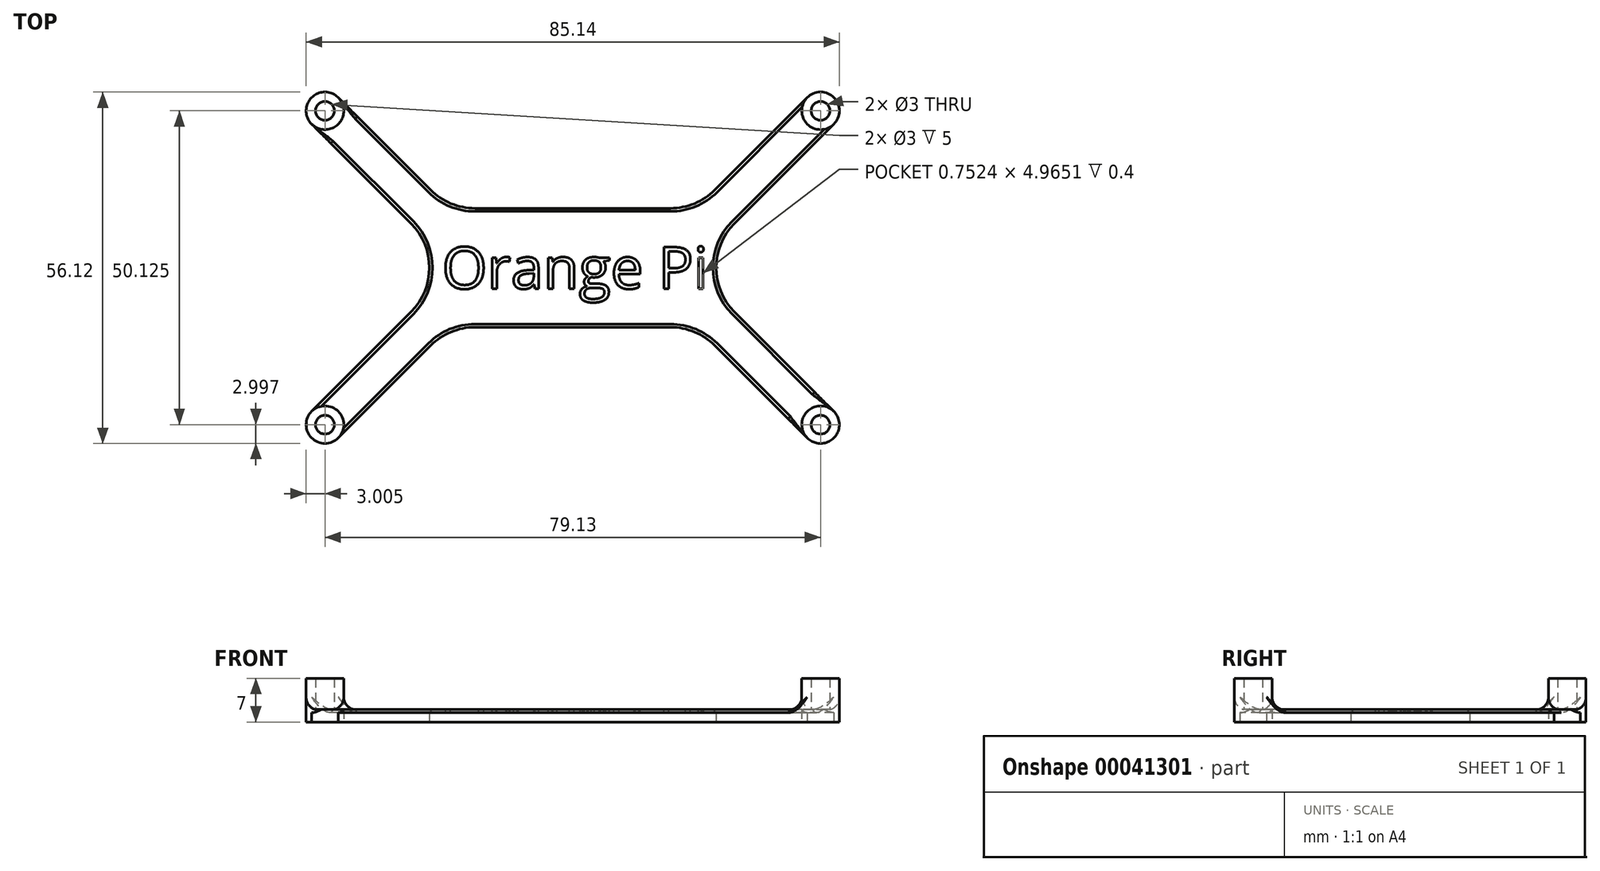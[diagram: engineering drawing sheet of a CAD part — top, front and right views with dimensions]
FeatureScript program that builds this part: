
annotation { "Feature Type Name" : "Feature", "Feature Type Description" : "" }
export const myFeature = defineFeature(function(context is Context, id is Id, definition is map)
    precondition{}
    {
        {
            var Q0;
            Q0=qCreatedBy(makeId("Top.planeOp"),FACE);
            var sketch = newSketch(context, id + "F0", { "sketchPlane" : qUnion([Q0])});
            skLineSegment(sketch, "E0", {"start": v(0, 77.14) * mm, "end": v(0, -73.03) * mm, "construction": true});
            skLineSegment(sketch, "E1", {"start": v(-119.62, 0) * mm, "end": v(131.14, 0) * mm, "construction": true});
            skCircle(sketch, "E2", {"center": v(-39.56, 25.06) * mm, "radius": 3 * mm});
            skLineSegment(sketch, "E3", {"start": v(-37.44, 27.18) * mm, "end": v(-22.69, 12.43) * mm});
            skLineSegment(sketch, "E4", {"start": v(-15.62, 9.5) * mm, "end": v(0, 9.5) * mm});
            skLineSegment(sketch, "E5", {"start": v(-41.69, 22.94) * mm, "end": v(-25.82, 7.07) * mm});
            skCircle(sketch, "E6.MirrorC", {"center": v(39.57, 25.06) * mm, "radius": 3 * mm});
            skLineSegment(sketch, "E7.MirrorCS", {"start": v(37.44, 27.18) * mm, "end": v(22.69, 12.43) * mm});
            skLineSegment(sketch, "E8.MirrorCS", {"start": v(41.69, 22.94) * mm, "end": v(25.82, 7.07) * mm});
            skLineSegment(sketch, "E9.MirrorCS", {"start": v(15.62, 9.5) * mm, "end": v(0, 9.5) * mm});
            skLineSegment(sketch, "E10.MirrorCS", {"start": v(15.62, -9.5) * mm, "end": v(0, -9.5) * mm});
            skLineSegment(sketch, "E11.MirrorCS", {"start": v(41.69, -22.94) * mm, "end": v(25.82, -7.07) * mm});
            skLineSegment(sketch, "E12.MirrorCS", {"start": v(37.44, -27.18) * mm, "end": v(22.69, -12.43) * mm});
            skCircle(sketch, "E13.MirrorC", {"center": v(39.57, -25.06) * mm, "radius": 3 * mm});
            skCircle(sketch, "E14.MirrorC", {"center": v(-39.56, -25.06) * mm, "radius": 3 * mm});
            skLineSegment(sketch, "E15.MirrorCS", {"start": v(-37.44, -27.18) * mm, "end": v(-22.69, -12.43) * mm});
            skLineSegment(sketch, "E16.MirrorCS", {"start": v(-15.62, -9.5) * mm, "end": v(0, -9.5) * mm});
            skLineSegment(sketch, "E17.MirrorCS", {"start": v(-41.69, -22.94) * mm, "end": v(-25.82, -7.07) * mm});
            skPoint(sketch, "E18.visualSharp", {"position": v(-19.76, 9.5) * mm});
            skArc(sketch, "E18.filletArc", {"start": v(-22.69, 12.43) * mm, "mid": v(-19.44, 10.26) * mm, "end": v(-15.62, 9.5) * mm});
            skPoint(sketch, "E19.visualSharp", {"position": v(-18.75, 0) * mm});
            skArc(sketch, "E19.filletArc", {"start": v(-25.82, -7.07) * mm, "mid": v(-22.89, 0) * mm, "end": v(-25.82, 7.07) * mm});
            skPoint(sketch, "E20.visualSharp", {"position": v(-19.76, -9.5) * mm});
            skArc(sketch, "E20.filletArc", {"start": v(-15.62, -9.5) * mm, "mid": v(-19.44, -10.26) * mm, "end": v(-22.69, -12.43) * mm});
            skPoint(sketch, "E21.visualSharp", {"position": v(19.76, -9.5) * mm});
            skArc(sketch, "E21.filletArc", {"start": v(22.69, -12.43) * mm, "mid": v(19.44, -10.26) * mm, "end": v(15.62, -9.5) * mm});
            skPoint(sketch, "E22.visualSharp", {"position": v(18.75, 0) * mm});
            skArc(sketch, "E22.filletArc", {"start": v(25.82, 7.07) * mm, "mid": v(22.89, 0) * mm, "end": v(25.82, -7.07) * mm});
            skPoint(sketch, "E23.visualSharp", {"position": v(19.76, 9.5) * mm});
            skArc(sketch, "E23.filletArc", {"start": v(15.62, 9.5) * mm, "mid": v(19.44, 10.26) * mm, "end": v(22.69, 12.43) * mm});
            skSolve(sketch);
        }
        {
            var Q0;
            {var subQ0=sQuery(id+"F0.wireOp",EDGE,"E2");var subQ2=makeQuery(id+"F0.imprint","INTERSECT",VERTEX,{"derivedFrom":[subQ0,sQuery(id+"F0.wireOp",EDGE,"E3")]});Q0=makeQuery(id+"F0.imprint","IMPRINT",FACE,{"disambiguationData":[TD([[makeQuery(id+"F0.imprint","IMPRINT",EDGE,{"disambiguationData":[TD([[subQ2,-1.0]])],"derivedFrom":subQ0}),1.0]])]});}
            var Q1;
            {var subQ0=sQuery(id+"F0.wireOp",EDGE,"E6.MirrorC");var subQ2=makeQuery(id+"F0.imprint","INTERSECT",VERTEX,{"derivedFrom":[subQ0,sQuery(id+"F0.wireOp",EDGE,"E7.MirrorCS")]});Q1=makeQuery(id+"F0.imprint","IMPRINT",FACE,{"disambiguationData":[TD([[makeQuery(id+"F0.imprint","IMPRINT",EDGE,{"disambiguationData":[TD([[subQ2,-1.0]])],"derivedFrom":subQ0}),-1.0]])]});}
            var Q2;
            {var subQ0=sQuery(id+"F0.wireOp",EDGE,"E13.MirrorC");var subQ2=makeQuery(id+"F0.imprint","INTERSECT",VERTEX,{"derivedFrom":[sQuery(id+"F0.wireOp",EDGE,"E11.MirrorCS"),subQ0]});Q2=makeQuery(id+"F0.imprint","IMPRINT",FACE,{"disambiguationData":[TD([[makeQuery(id+"F0.imprint","IMPRINT",EDGE,{"disambiguationData":[TD([[subQ2,1.0]])],"derivedFrom":subQ0}),1.0]])]});}
            var Q3;
            {var subQ0=sQuery(id+"F0.wireOp",EDGE,"E14.MirrorC");var subQ2=makeQuery(id+"F0.imprint","INTERSECT",VERTEX,{"derivedFrom":[subQ0,sQuery(id+"F0.wireOp",EDGE,"E15.MirrorCS")]});Q3=makeQuery(id+"F0.imprint","IMPRINT",FACE,{"disambiguationData":[TD([[makeQuery(id+"F0.imprint","IMPRINT",EDGE,{"disambiguationData":[TD([[subQ2,-1.0]])],"derivedFrom":subQ0}),-1.0]])]});}
            var Q4;
            {var subQ6=sQuery(id+"F0.wireOp",EDGE,"E3");Q4=makeQuery(id+"F0.imprint","IMPRINT",FACE,{"disambiguationData":[TD([[makeQuery(id+"F0.imprint","IMPRINT",EDGE,{"derivedFrom":subQ6}),-1.0]])]});}
            extrude(context, id + "F1", {"entities" : qUnion([Q0, Q1, Q2, Q3, Q4]), "depth" : 2 * mm});
        }
        {
            var Q0;
            Q0=makeQuery(id+"F1.opExtrude","CAP_FACE",FACE,{"disambiguationData":[OSD([sQuery(id+"F0.wireOp",EDGE,"E2"),sQuery(id+"F0.wireOp",EDGE,"E3"),sQuery(id+"F0.wireOp",EDGE,"E4"),sQuery(id+"F0.wireOp",EDGE,"E5"),sQuery(id+"F0.wireOp",EDGE,"E6.MirrorC"),sQuery(id+"F0.wireOp",EDGE,"E7.MirrorCS"),sQuery(id+"F0.wireOp",EDGE,"E8.MirrorCS"),sQuery(id+"F0.wireOp",EDGE,"E9.MirrorCS"),sQuery(id+"F0.wireOp",EDGE,"E10.MirrorCS"),sQuery(id+"F0.wireOp",EDGE,"E11.MirrorCS"),sQuery(id+"F0.wireOp",EDGE,"E12.MirrorCS"),sQuery(id+"F0.wireOp",EDGE,"E13.MirrorC"),sQuery(id+"F0.wireOp",EDGE,"E14.MirrorC"),sQuery(id+"F0.wireOp",EDGE,"E15.MirrorCS"),sQuery(id+"F0.wireOp",EDGE,"E16.MirrorCS"),sQuery(id+"F0.wireOp",EDGE,"E17.MirrorCS"),sQuery(id+"F0.wireOp",EDGE,"E18.filletArc"),sQuery(id+"F0.wireOp",EDGE,"E19.filletArc"),sQuery(id+"F0.wireOp",EDGE,"E20.filletArc"),sQuery(id+"F0.wireOp",EDGE,"E21.filletArc"),sQuery(id+"F0.wireOp",EDGE,"E22.filletArc"),sQuery(id+"F0.wireOp",EDGE,"E23.filletArc")])],"isStart":false});
            var sketch = newSketch(context, id + "F2", { "sketchPlane" : qUnion([Q0])});
            skCircle(sketch, "E24.0", {"center": v(-39.56, 25.06) * mm, "radius": 3 * mm});
            skCircle(sketch, "E24.1", {"center": v(-39.56, -25.06) * mm, "radius": 3 * mm});
            skCircle(sketch, "E24.2", {"center": v(39.57, -25.06) * mm, "radius": 3 * mm});
            skCircle(sketch, "E24.3", {"center": v(39.57, 25.06) * mm, "radius": 3 * mm});
            skCircle(sketch, "E25", {"center": v(-39.56, 25.06) * mm, "radius": 1.5 * mm});
            skCircle(sketch, "E26", {"center": v(39.57, 25.06) * mm, "radius": 1.5 * mm});
            skCircle(sketch, "E27", {"center": v(39.57, -25.06) * mm, "radius": 1.5 * mm});
            skCircle(sketch, "E28", {"center": v(-39.56, -25.06) * mm, "radius": 1.5 * mm});
            skText(sketch, "E29", { "text": "Orange Pi", "fontName": "OpenSans-Regular.ttf"});
            skLineSegment(sketch, "E30", {"start": v(0, 0) * mm, "end": v(22.89, 0) * mm, "construction": true});
            skLineSegment(sketch, "E31", {"start": v(0, 0) * mm, "end": v(0, 9.5) * mm, "construction": true});
            skPoint(sketch, "E32", {"position": v(20.89, 0) * mm});
            const initialGuessF2  = {"E29": [-0.02089, -0.00334, 1, 0, 0.00668]};
            skSetInitialGuess(sketch, initialGuessF2);
            skSolve(sketch);
        }
        {
            var Q0;
            Q0=makeQuery(id+"F2.imprint","IMPRINT",FACE,{"disambiguationData":[TD([[makeQuery(id+"F2.imprint","IMPRINT",EDGE,{"derivedFrom":sQuery(id+"F2.wireOp",EDGE,"E25")}),-1.0]])]});
            var Q1;
            Q1=makeQuery(id+"F2.imprint","IMPRINT",FACE,{"disambiguationData":[TD([[makeQuery(id+"F2.imprint","IMPRINT",EDGE,{"derivedFrom":sQuery(id+"F2.wireOp",EDGE,"E28")}),-1.0]])]});
            var Q2;
            Q2=makeQuery(id+"F2.imprint","IMPRINT",FACE,{"disambiguationData":[TD([[makeQuery(id+"F2.imprint","IMPRINT",EDGE,{"derivedFrom":sQuery(id+"F2.wireOp",EDGE,"E27")}),-1.0]])]});
            var Q3;
            Q3=makeQuery(id+"F2.imprint","IMPRINT",FACE,{"disambiguationData":[TD([[makeQuery(id+"F2.imprint","IMPRINT",EDGE,{"derivedFrom":sQuery(id+"F2.wireOp",EDGE,"E26")}),-1.0]])]});
            extrude(context, id + "F3", {"entities" : qUnion([Q0, Q1, Q2, Q3]), "operationType" : NewBodyOperationType.ADD, "depth" : 5 * mm});
        }
        {
            var Q0;
            Q0=makeQuery(id+"F3.opExtrude","CAP_EDGE",EDGE,{"disambiguationData":[OSD([sQuery(id+"F2.wireOp",EDGE,"E24.3")])],"isStart":true});
            var Q1;
            Q1=makeQuery(id+"F3.opExtrude","CAP_EDGE",EDGE,{"disambiguationData":[OSD([sQuery(id+"F2.wireOp",EDGE,"E24.2")])],"isStart":true});
            var Q2;
            Q2=makeQuery(id+"F3.opExtrude","CAP_EDGE",EDGE,{"disambiguationData":[OSD([sQuery(id+"F2.wireOp",EDGE,"E24.1")])],"isStart":true});
            var Q3;
            Q3=makeQuery(id+"F3.opExtrude","CAP_EDGE",EDGE,{"disambiguationData":[OSD([sQuery(id+"F2.wireOp",EDGE,"E24.0")])],"isStart":true});
            fillet(context, id + "F4", {"entities" : qUnion([Q0, Q1, Q2, Q3]), "radius" : 2 * mm, "tangentPropagation" : true, "allowEdgeOverflow" : false});
        }
        {
            var Q0;
            Q0=makeQuery(id+"F1.opExtrude","CAP_EDGE",EDGE,{"disambiguationData":[OSD([sQuery(id+"F0.wireOp",EDGE,"E11.MirrorCS")])],"isStart":false});
            var Q1;
            Q1=makeQuery(id+"F1.opExtrude","CAP_EDGE",EDGE,{"disambiguationData":[OSD([sQuery(id+"F0.wireOp",EDGE,"E7.MirrorCS")])],"isStart":false});
            var Q2;
            Q2=makeQuery(id+"F1.opExtrude","CAP_EDGE",EDGE,{"disambiguationData":[OSD([sQuery(id+"F0.wireOp",EDGE,"E19.filletArc")])],"isStart":false});
            var Q3;
            Q3=makeQuery(id+"F1.opExtrude","CAP_EDGE",EDGE,{"disambiguationData":[OSD([sQuery(id+"F0.wireOp",EDGE,"E10.MirrorCS"),sQuery(id+"F0.wireOp",EDGE,"E16.MirrorCS")])],"isStart":false});
            chamfer(context, id + "F5", {"entities" : qUnion([Q0, Q1, Q2, Q3]), "width" : 0.5 * mm, "tangentPropagation" : true});
        }
        {
            var Q0;
            Q0=makeQuery(id+"F2.imprint","IMPRINT",FACE,{"disambiguationData":[TD([[makeQuery(id+"F2.imprint","IMPRINT",EDGE,{"derivedFrom":sQuery(id+"F2.wireOp",EDGE,"E29.sketch_text.stroke-0")}),-1.0]])]});
            var Q1;
            Q1=makeQuery(id+"F2.imprint","IMPRINT",FACE,{"disambiguationData":[TD([[makeQuery(id+"F2.imprint","IMPRINT",EDGE,{"derivedFrom":sQuery(id+"F2.wireOp",EDGE,"E29.sketch_text.stroke-16")}),-1.0]])]});
            var Q2;
            Q2=makeQuery(id+"F2.imprint","IMPRINT",FACE,{"disambiguationData":[TD([[makeQuery(id+"F2.imprint","IMPRINT",EDGE,{"derivedFrom":sQuery(id+"F2.wireOp",EDGE,"E29.sketch_text.stroke-29")}),-1.0]])]});
            var Q3;
            Q3=makeQuery(id+"F2.imprint","IMPRINT",FACE,{"disambiguationData":[TD([[makeQuery(id+"F2.imprint","IMPRINT",EDGE,{"derivedFrom":sQuery(id+"F2.wireOp",EDGE,"E29.sketch_text.stroke-56")}),-1.0]])]});
            var Q4;
            Q4=makeQuery(id+"F2.imprint","IMPRINT",FACE,{"disambiguationData":[TD([[makeQuery(id+"F2.imprint","IMPRINT",EDGE,{"derivedFrom":sQuery(id+"F2.wireOp",EDGE,"E29.sketch_text.stroke-136")}),-1.0]])]});
            var Q5;
            Q5=makeQuery(id+"F2.imprint","IMPRINT",FACE,{"disambiguationData":[TD([[makeQuery(id+"F2.imprint","IMPRINT",EDGE,{"derivedFrom":sQuery(id+"F2.wireOp",EDGE,"E29.sketch_text.stroke-151")}),-1.0]])]});
            var Q6;
            Q6=makeQuery(id+"F2.imprint","IMPRINT",FACE,{"disambiguationData":[TD([[makeQuery(id+"F2.imprint","IMPRINT",EDGE,{"derivedFrom":sQuery(id+"F2.wireOp",EDGE,"E29.sketch_text.stroke-155")}),-1.0]])]});
            var Q7;
            Q7=makeQuery(id+"F2.imprint","IMPRINT",FACE,{"disambiguationData":[TD([[makeQuery(id+"F2.imprint","IMPRINT",EDGE,{"derivedFrom":sQuery(id+"F2.wireOp",EDGE,"E29.sketch_text.stroke-117")}),-1.0]])]});
            var Q8;
            Q8=makeQuery(id+"F2.imprint","IMPRINT",FACE,{"disambiguationData":[TD([[makeQuery(id+"F2.imprint","IMPRINT",EDGE,{"derivedFrom":sQuery(id+"F2.wireOp",EDGE,"E29.sketch_text.stroke-73")}),-1.0]])]});
            extrude(context, id + "F6", {"entities" : qUnion([Q0, Q1, Q2, Q3, Q4, Q5, Q6, Q7, Q8]), "operationType" : NewBodyOperationType.REMOVE, "oppositeDirection" : true, "depth" : 0.4 * mm});
        }
    });
